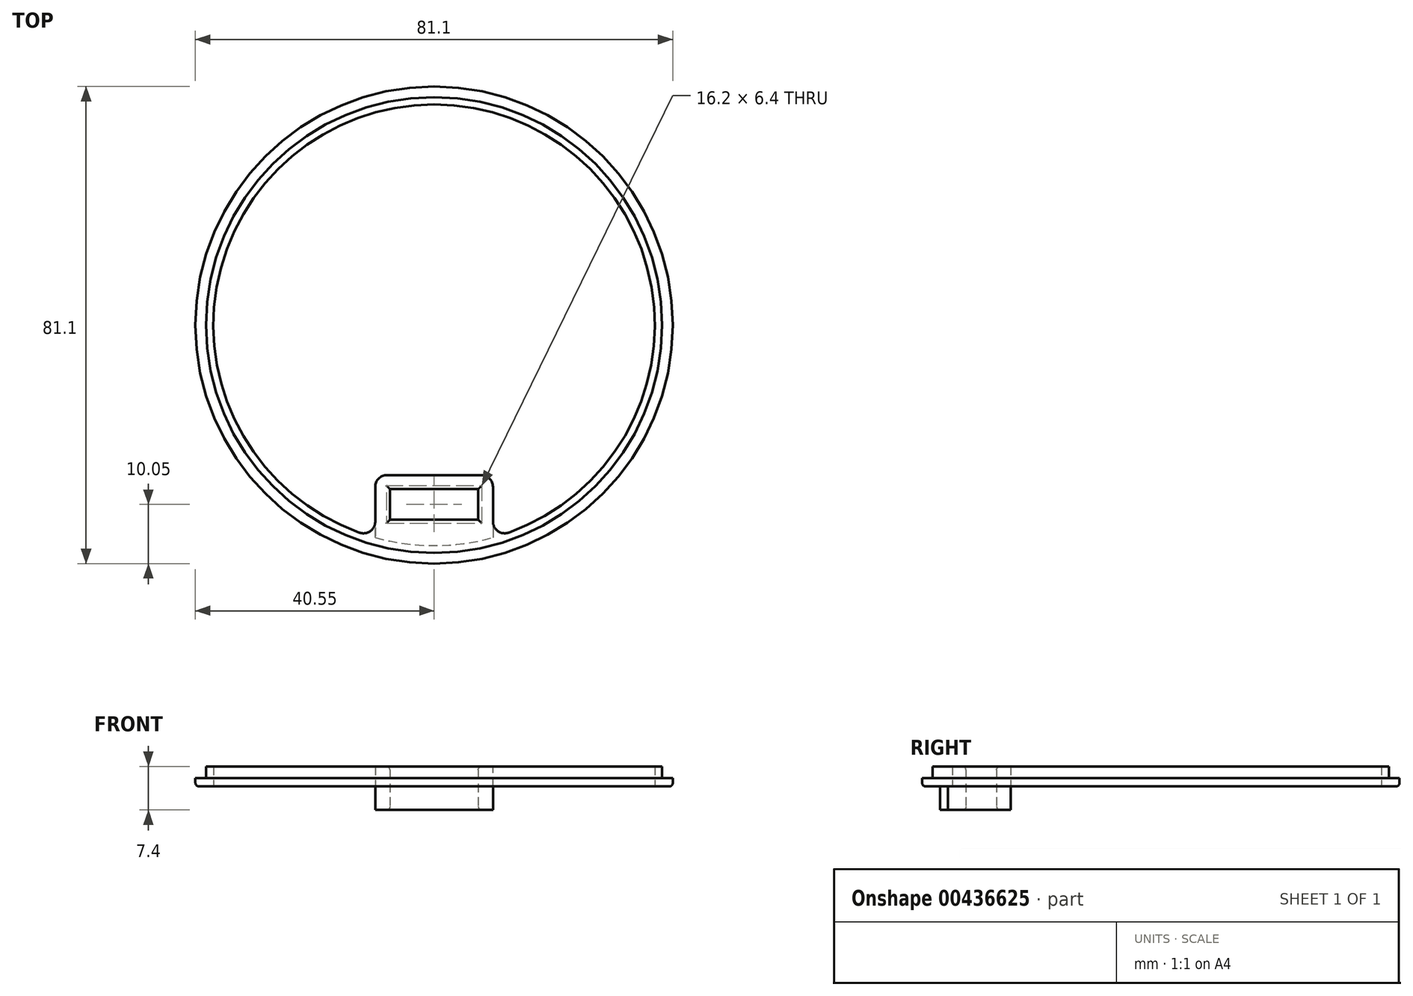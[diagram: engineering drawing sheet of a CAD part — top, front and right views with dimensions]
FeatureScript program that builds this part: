
annotation { "Feature Type Name" : "Feature", "Feature Type Description" : "" }
export const myFeature = defineFeature(function(context is Context, id is Id, definition is map)
    precondition{}
    {
        {
            var Q0;
            Q0=qCreatedBy(makeId("Top.planeOp"),FACE);
            var sketch = newSketch(context, id + "F0", { "sketchPlane" : qUnion([Q0])});
            skCircle(sketch, "E0", {"center": v(0, 0) * mm, "radius": 40.55 * mm});
            skCircle(sketch, "E1", {"center": v(0, 0) * mm, "radius": 38.75 * mm});
            skCircle(sketch, "E2", {"center": v(0, 0) * mm, "radius": 37.5 * mm});
            skLineSegment(sketch, "E3.bottom", {"start": v(7.5, -27.9) * mm, "end": v(-7.5, -27.9) * mm});
            skLineSegment(sketch, "E3.top", {"start": v(7.5, -33.1) * mm, "end": v(-7.5, -33.1) * mm});
            skLineSegment(sketch, "E3.left", {"start": v(7.5, -27.9) * mm, "end": v(7.5, -33.1) * mm});
            skLineSegment(sketch, "E3.right", {"start": v(-7.5, -27.9) * mm, "end": v(-7.5, -33.1) * mm});
            skPoint(sketch, "E3.middle", {"position": v(0, -30.5) * mm});
            skLineSegment(sketch, "E4.bottom", {"start": v(10, -25.5) * mm, "end": v(-10, -25.5) * mm});
            skLineSegment(sketch, "E4.top", {"start": v(10, -39) * mm, "end": v(-10, -39) * mm});
            skLineSegment(sketch, "E4.left", {"start": v(10, -25.5) * mm, "end": v(10, -39) * mm});
            skLineSegment(sketch, "E4.right", {"start": v(-10, -25.5) * mm, "end": v(-10, -39) * mm});
            skSolve(sketch);
        }
        {
            var Q0;
            Q0=makeQuery(id+"F0.imprint","IMPRINT",FACE,{"disambiguationData":[TD([[makeQuery(id+"F0.imprint","IMPRINT",EDGE,{"derivedFrom":sQuery(id+"F0.wireOp",EDGE,"E0")}),1.0]])]});
            var Q1;
            {var subQ0=sQuery(id+"F0.wireOp",EDGE,"E4.left");var subQ1=sQuery(id+"F0.wireOp",EDGE,"E1");var subQ2=makeQuery(id+"F0.imprint","INTERSECT",VERTEX,{"derivedFrom":[subQ1,subQ0]});Q1=makeQuery(id+"F0.imprint","IMPRINT",FACE,{"disambiguationData":[TD([[makeQuery(id+"F0.imprint","IMPRINT",EDGE,{"disambiguationData":[TD([[subQ2,-1.0]])],"derivedFrom":subQ1}),1.0]])]});}
            var Q2;
            Q2=makeQuery(id+"F0.imprint","IMPRINT",FACE,{"disambiguationData":[TD([[makeQuery(id+"F0.imprint","IMPRINT",EDGE,{"derivedFrom":sQuery(id+"F0.wireOp",EDGE,"E3.bottom")}),-1.0]])]});
            var Q3;
            {var subQ0=sQuery(id+"F0.wireOp",EDGE,"E4.left");var subQ1=sQuery(id+"F0.wireOp",EDGE,"E1");var subQ2=makeQuery(id+"F0.imprint","INTERSECT",VERTEX,{"derivedFrom":[subQ1,subQ0]});Q3=makeQuery(id+"F0.imprint","IMPRINT",FACE,{"disambiguationData":[TD([[makeQuery(id+"F0.imprint","IMPRINT",EDGE,{"disambiguationData":[TD([[subQ2,1.0]])],"derivedFrom":subQ1}),1.0]])]});}
            var Q4;
            {var subQ5=sQuery(id+"F0.wireOp",EDGE,"E4.top");Q4=makeQuery(id+"F0.imprint","IMPRINT",FACE,{"disambiguationData":[TD([[makeQuery(id+"F0.imprint","IMPRINT",EDGE,{"derivedFrom":subQ5}),-1.0]])]});}
            extrude(context, id + "F1", {"entities" : qUnion([Q0, Q1, Q2, Q3, Q4]), "depth" : 1.4 * mm});
        }
        {
            var Q0;
            {var subQ0=sQuery(id+"F0.wireOp",EDGE,"E4.left");var subQ1=sQuery(id+"F0.wireOp",EDGE,"E1");var subQ2=makeQuery(id+"F0.imprint","INTERSECT",VERTEX,{"derivedFrom":[subQ1,subQ0]});Q0=makeQuery(id+"F0.imprint","IMPRINT",FACE,{"disambiguationData":[TD([[makeQuery(id+"F0.imprint","IMPRINT",EDGE,{"disambiguationData":[TD([[subQ2,-1.0]])],"derivedFrom":subQ1}),1.0]])]});}
            var Q1;
            {var subQ0=sQuery(id+"F0.wireOp",EDGE,"E4.left");var subQ1=sQuery(id+"F0.wireOp",EDGE,"E1");var subQ2=makeQuery(id+"F0.imprint","INTERSECT",VERTEX,{"derivedFrom":[subQ1,subQ0]});Q1=makeQuery(id+"F0.imprint","IMPRINT",FACE,{"disambiguationData":[TD([[makeQuery(id+"F0.imprint","IMPRINT",EDGE,{"disambiguationData":[TD([[subQ2,1.0]])],"derivedFrom":subQ1}),1.0]])]});}
            var Q2;
            Q2=makeQuery(id+"F0.imprint","IMPRINT",FACE,{"disambiguationData":[TD([[makeQuery(id+"F0.imprint","IMPRINT",EDGE,{"derivedFrom":sQuery(id+"F0.wireOp",EDGE,"E3.bottom")}),-1.0]])]});
            extrude(context, id + "F2", {"entities" : qUnion([Q0, Q1, Q2]), "operationType" : NewBodyOperationType.ADD, "depth" : 3.4 * mm});
        }
        {
            var Q0;
            Q0=makeQuery(id+"F0.imprint","IMPRINT",FACE,{"disambiguationData":[TD([[makeQuery(id+"F0.imprint","IMPRINT",EDGE,{"derivedFrom":sQuery(id+"F0.wireOp",EDGE,"E3.bottom")}),-1.0]])]});
            extrude(context, id + "F3", {"entities" : qUnion([Q0]), "operationType" : NewBodyOperationType.ADD, "oppositeDirection" : true, "depth" : 4 * mm});
        }
        {
            var Q0;
            Q0=makeQuery(id+"F1.opExtrude","CAP_EDGE",EDGE,{"disambiguationData":[OSD([sQuery(id+"F0.wireOp",EDGE,"E0")])],"isStart":true});
            fillet(context, id + "F4", {"entities" : qUnion([Q0]), "radius" : .6 * mm, "tangentPropagation" : true, "allowEdgeOverflow" : false});
        }
        {
            var Q0;
            {var subQ0=sQuery(id+"F0.wireOp",EDGE,"E4.right");var subQ1=sQuery(id+"F0.wireOp",EDGE,"E4.bottom");Q0=makeQuery(id+"F3.boolean.opBoolean","MERGE",EDGE,{"derivedFrom":[makeQuery(id+"F2.boolean.opBoolean","MERGE",EDGE,{"derivedFrom":[makeQuery(id+"F1.opExtrude","SWEPT_EDGE",EDGE,{"disambiguationData":[OSD([subQ1,subQ0])]}),makeQuery(id+"F2.opExtrude","SWEPT_EDGE",EDGE,{"disambiguationData":[OSD([subQ1,subQ0])]})]}),makeQuery(id+"F3.opExtrude","SWEPT_EDGE",EDGE,{"disambiguationData":[OSD([subQ1,subQ0])]})]});}
            var Q1;
            {var subQ0=sQuery(id+"F0.wireOp",EDGE,"E4.left");var subQ1=sQuery(id+"F0.wireOp",EDGE,"E4.bottom");Q1=makeQuery(id+"F3.boolean.opBoolean","MERGE",EDGE,{"derivedFrom":[makeQuery(id+"F2.boolean.opBoolean","MERGE",EDGE,{"derivedFrom":[makeQuery(id+"F1.opExtrude","SWEPT_EDGE",EDGE,{"disambiguationData":[OSD([subQ1,subQ0])]}),makeQuery(id+"F2.opExtrude","SWEPT_EDGE",EDGE,{"disambiguationData":[OSD([subQ1,subQ0])]})]}),makeQuery(id+"F3.opExtrude","SWEPT_EDGE",EDGE,{"disambiguationData":[OSD([subQ1,subQ0])]})]});}
            var Q2;
            {var subQ0=sQuery(id+"F0.wireOp",EDGE,"E4.left");var subQ1=sQuery(id+"F0.wireOp",EDGE,"E2");Q2=makeQuery(id+"F2.boolean.opBoolean","MERGE",EDGE,{"derivedFrom":[makeQuery(id+"F1.opExtrude","SWEPT_EDGE",EDGE,{"disambiguationData":[OSD([subQ1,subQ0])]}),makeQuery(id+"F2.opExtrude","SWEPT_EDGE",EDGE,{"disambiguationData":[OSD([subQ1,subQ0])]})]});}
            var Q3;
            {var subQ0=sQuery(id+"F0.wireOp",EDGE,"E4.right");var subQ1=sQuery(id+"F0.wireOp",EDGE,"E2");Q3=makeQuery(id+"F2.boolean.opBoolean","MERGE",EDGE,{"derivedFrom":[makeQuery(id+"F1.opExtrude","SWEPT_EDGE",EDGE,{"disambiguationData":[OSD([subQ1,subQ0])]}),makeQuery(id+"F2.opExtrude","SWEPT_EDGE",EDGE,{"disambiguationData":[OSD([subQ1,subQ0])]})]});}
            fillet(context, id + "F5", {"entities" : qUnion([Q0, Q1, Q2, Q3]), "radius" : 2 * mm, "tangentPropagation" : true, "allowEdgeOverflow" : false});
        }
        {
            var Q0;
            Q0=makeQuery(id+"F2.opExtrude","CAP_EDGE",EDGE,{"disambiguationData":[OSD([sQuery(id+"F0.wireOp",EDGE,"E3.left")])],"isStart":false});
            var Q1;
            Q1=makeQuery(id+"F2.opExtrude","CAP_EDGE",EDGE,{"disambiguationData":[OSD([sQuery(id+"F0.wireOp",EDGE,"E3.bottom")])],"isStart":false});
            var Q2;
            Q2=makeQuery(id+"F2.opExtrude","CAP_EDGE",EDGE,{"disambiguationData":[OSD([sQuery(id+"F0.wireOp",EDGE,"E3.right")])],"isStart":false});
            var Q3;
            Q3=makeQuery(id+"F2.opExtrude","CAP_EDGE",EDGE,{"disambiguationData":[OSD([sQuery(id+"F0.wireOp",EDGE,"E3.top")])],"isStart":false});
            var Q4;
            Q4=makeQuery(id+"F3.opExtrude","CAP_EDGE",EDGE,{"disambiguationData":[OSD([sQuery(id+"F0.wireOp",EDGE,"E3.right")])],"isStart":false});
            var Q5;
            Q5=makeQuery(id+"F3.opExtrude","CAP_EDGE",EDGE,{"disambiguationData":[OSD([sQuery(id+"F0.wireOp",EDGE,"E3.bottom")])],"isStart":false});
            var Q6;
            Q6=makeQuery(id+"F3.opExtrude","CAP_EDGE",EDGE,{"disambiguationData":[OSD([sQuery(id+"F0.wireOp",EDGE,"E3.left")])],"isStart":false});
            var Q7;
            Q7=makeQuery(id+"F3.opExtrude","CAP_EDGE",EDGE,{"disambiguationData":[OSD([sQuery(id+"F0.wireOp",EDGE,"E3.top")])],"isStart":false});
            fillet(context, id + "F6", {"entities" : qUnion([Q0, Q1, Q2, Q3, Q4, Q5, Q6, Q7]), "radius" : .6 * mm, "tangentPropagation" : true, "allowEdgeOverflow" : false});
        }
    });
